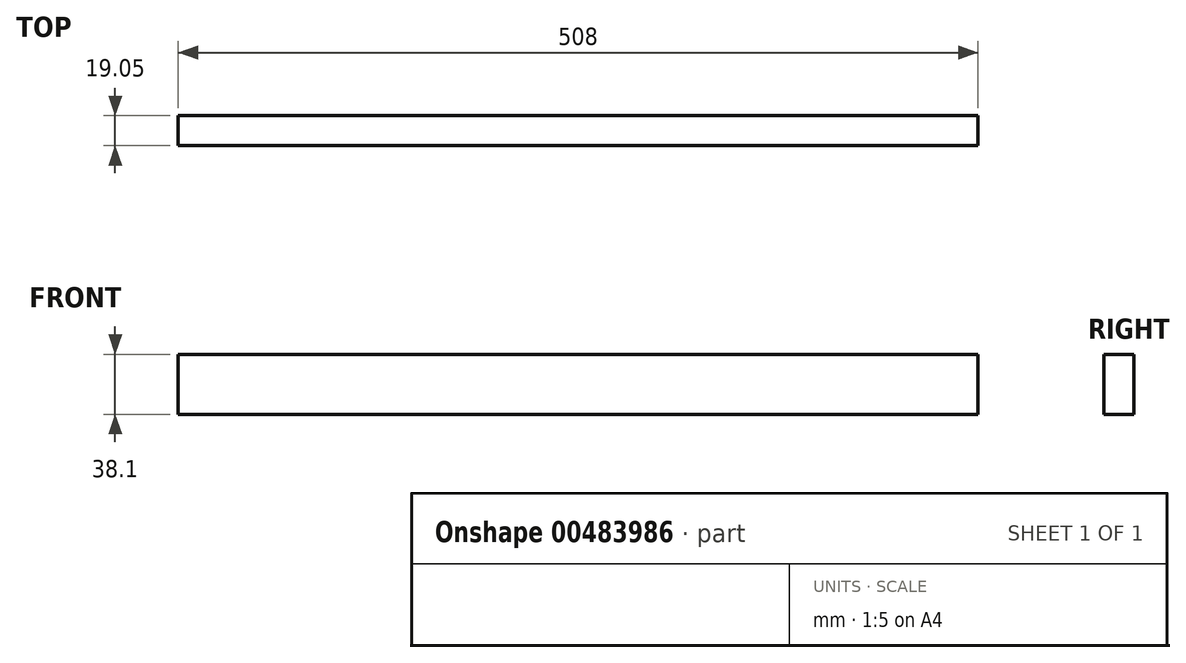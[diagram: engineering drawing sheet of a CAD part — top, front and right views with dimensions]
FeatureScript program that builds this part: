
annotation { "Feature Type Name" : "Feature", "Feature Type Description" : "" }
export const myFeature = defineFeature(function(context is Context, id is Id, definition is map)
    precondition{}
    {
        {
            var Q0;
            Q0=qCreatedBy(makeId("Front.planeOp"),FACE);
            var sketch = newSketch(context, id + "F0", { "sketchPlane" : qUnion([Q0])});
            skLineSegment(sketch, "E0.bottom", {"start": v(254, -19.05) * mm, "end": v(-254, -19.05) * mm});
            skLineSegment(sketch, "E0.top", {"start": v(254, 19.05) * mm, "end": v(-254, 19.05) * mm});
            skLineSegment(sketch, "E0.left", {"start": v(254, -19.05) * mm, "end": v(254, 19.05) * mm});
            skLineSegment(sketch, "E0.right", {"start": v(-254, -19.05) * mm, "end": v(-254, 19.05) * mm});
            skPoint(sketch, "E0.middle", {"position": v(0, 0) * mm});
            skSolve(sketch);
        }
        {
            var Q0;
            Q0 = qSketchRegion(id + "F0", true);
            extrude(context, id + "F1", {"entities" : qUnion([Q0]), "depth" : 19.05 * mm});
        }
    });
